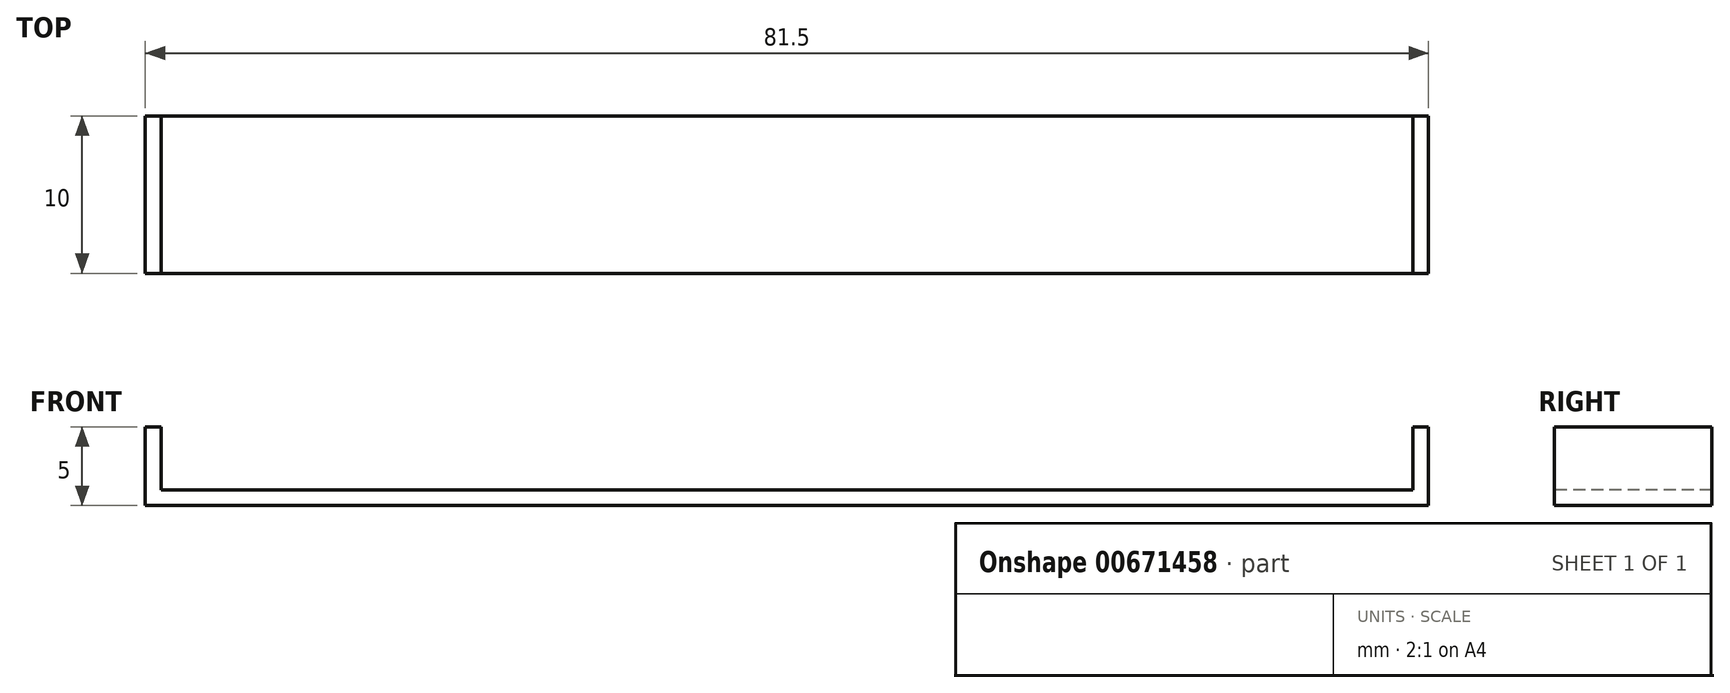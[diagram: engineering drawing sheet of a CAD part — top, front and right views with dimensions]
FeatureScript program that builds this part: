
annotation { "Feature Type Name" : "Feature", "Feature Type Description" : "" }
export const myFeature = defineFeature(function(context is Context, id is Id, definition is map)
    precondition{}
    {
        {
            var Q0;
            Q0=qCreatedBy(makeId("Top.planeOp"),FACE);
            var sketch = newSketch(context, id + "F0", { "sketchPlane" : qUnion([Q0])});
            skLineSegment(sketch, "E0.bottom", {"start": v(0, 0) * mm, "end": v(-79.5, 0) * mm});
            skLineSegment(sketch, "E0.top", {"start": v(0, 10) * mm, "end": v(-79.5, 10) * mm});
            skLineSegment(sketch, "E0.left", {"start": v(0, 0) * mm, "end": v(0, 10) * mm});
            skLineSegment(sketch, "E0.right", {"start": v(-79.5, 0) * mm, "end": v(-79.5, 10) * mm});
            skLineSegment(sketch, "E1.bottom", {"start": v(-79.5, 10) * mm, "end": v(-80.5, 10) * mm});
            skLineSegment(sketch, "E1.top", {"start": v(-79.5, 0) * mm, "end": v(-80.5, 0) * mm});
            skLineSegment(sketch, "E1.left", {"start": v(-79.5, 10) * mm, "end": v(-79.5, 0) * mm});
            skLineSegment(sketch, "E1.right", {"start": v(-80.5, 10) * mm, "end": v(-80.5, 0) * mm});
            skLineSegment(sketch, "E2.bottom", {"start": v(0, 10) * mm, "end": v(1, 10) * mm});
            skLineSegment(sketch, "E2.top", {"start": v(0, 0) * mm, "end": v(1, 0) * mm});
            skLineSegment(sketch, "E2.left", {"start": v(0, 10) * mm, "end": v(0, 0) * mm});
            skLineSegment(sketch, "E2.right", {"start": v(1, 10) * mm, "end": v(1, 0) * mm});
            skSolve(sketch);
        }
        {
            var Q0;
            Q0 = qSketchRegion(id + "F0", true);
            extrude(context, id + "F1", {"entities" : qUnion([Q0]), "depth" : 1 * mm, "offsetDistance" : 25 * mm});
        }
        {
            var Q0;
            Q0=makeQuery(id+"F0.imprint","IMPRINT",FACE,{"disambiguationData":[TD([[makeQuery(id+"F0.imprint","IMPRINT",EDGE,{"derivedFrom":sQuery(id+"F0.wireOp",EDGE,"E1.bottom")}),1.0]])]});
            var Q1;
            Q1=makeQuery(id+"F0.imprint","IMPRINT",FACE,{"disambiguationData":[TD([[makeQuery(id+"F0.imprint","IMPRINT",EDGE,{"derivedFrom":sQuery(id+"F0.wireOp",EDGE,"E2.bottom")}),-1.0]])]});
            extrude(context, id + "F2", {"entities" : qUnion([Q0, Q1]), "operationType" : NewBodyOperationType.ADD, "depth" : 5 * mm, "offsetDistance" : 25 * mm});
        }
    });
